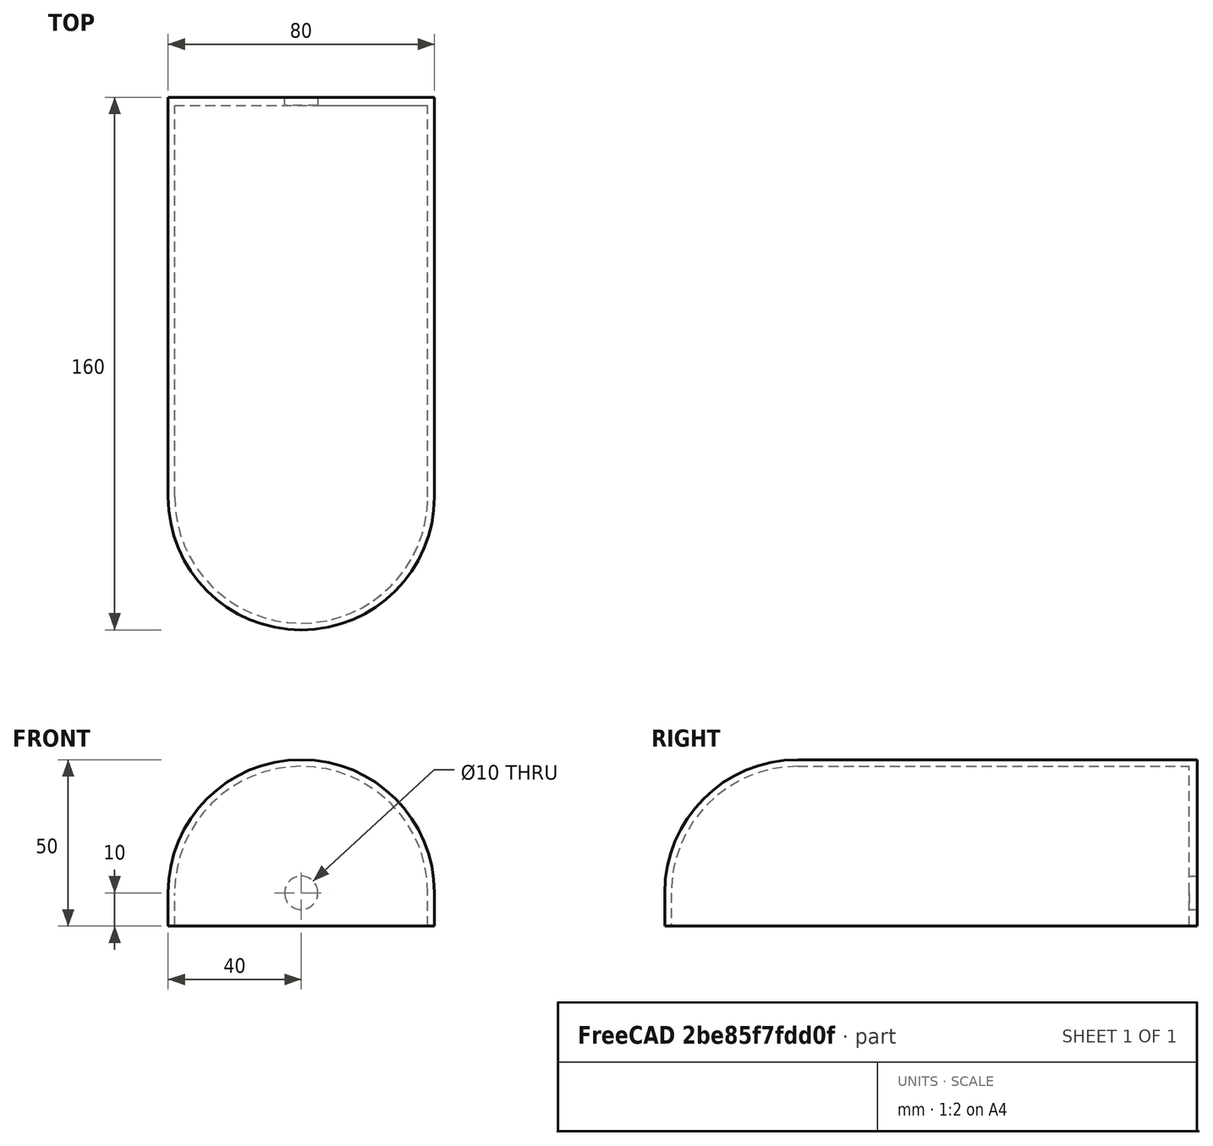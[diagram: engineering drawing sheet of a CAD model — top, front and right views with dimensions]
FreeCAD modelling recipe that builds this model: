
FCSTD DOCUMENT  (FreeCAD 0.20R29177 +426 (Git))
Label: Cabeza de lampara
License: All rights reserved
LicenseURL: http://en.wikipedia.org/wiki/All_rights_reserved
objects: Part::Cylinder×7, Part::Cut×6, Part::Box×3, Part::Sphere×2, Part::MultiFuse×2
note: 20 computed .brp shape members not serialized (recipe doc carries the construction recipe); baked Part::Feature solids carry a one-line shape summary decoded from their .brp

FEATURE [Part::Box] Box  label="Soporte parte inferior"
  AttacherType = Attacher::AttachEngine3D
  Height = 10
  Length = 76
  Placement = pos=(2,17.5,30) rot=(0,0,1;0rad)
  Width = 2.5
FEATURE [Part::Cylinder] Cylinder  label="Cilindro superior mayor"
  Angle = 180
  AttacherType = Attacher::AttachEngine3D
  FirstAngle = 0
  Height = 120
  Placement = pos=(40,20,40) rot=(1,0,0;1.5708rad)
  Radius = 40
  SecondAngle = 0
FEATURE [Part::Sphere] Sphere  label="Esfera mayor"
  Angle1 = -90
  Angle2 = 90
  Angle3 = 180
  AttacherType = Attacher::AttachEngine3D
  Placement = pos=(40,-100,40) rot=(1,0,0;1.5708rad)
  Radius = 40
FEATURE [Part::Box] Box001  label="Rectangulo mayor"
  AttacherType = Attacher::AttachEngine3D
  Height = 10
  Length = 80
  Placement = pos=(0,-100,30) rot=(0,0,1;0rad)
  Width = 120
FEATURE [Part::Cylinder] Cylinder001  label="Cilindro mayor"
  Angle = 180
  AttacherType = Attacher::AttachEngine3D
  FirstAngle = 0
  Height = 10
  Placement = pos=(40,-100,30) rot=(0,0,1;3.14159rad)
  Radius = 40
  SecondAngle = 0
FEATURE [Part::Cylinder] Cylinder002  label="Cilindro menor"
  Angle = 180
  AttacherType = Attacher::AttachEngine3D
  FirstAngle = 0
  Height = 10
  Placement = pos=(40,-100,30) rot=(0,0,1;3.14159rad)
  Radius = 38
  SecondAngle = 0
FEATURE [Part::Box] Box002  label="Rectangulo menor"
  AttacherType = Attacher::AttachEngine3D
  Height = 10
  Length = 76
  Placement = pos=(2,-100,30) rot=(0,0,1;0rad)
  Width = 120
FEATURE [Part::Sphere] Sphere001  label="Esfera menor"
  Angle1 = -90
  Angle2 = 90
  Angle3 = 180
  AttacherType = Attacher::AttachEngine3D
  Placement = pos=(40,-100,40) rot=(1,0,0;1.5708rad)
  Radius = 38
FEATURE [Part::Cylinder] Cylinder003  label="Cilindro superior menor"
  Angle = 180
  AttacherType = Attacher::AttachEngine3D
  FirstAngle = 0
  Height = 120
  Placement = pos=(40,20,40) rot=(1,0,0;1.5708rad)
  Radius = 38
  SecondAngle = 0
FEATURE [Part::Cut] Cut  label="Bordes"
  Base = -> Box001
  Tool = -> Box002
FEATURE [Part::Cut] Cut001  label="Techo"
  Base = -> Cylinder
  Tool = -> Cylinder003
FEATURE [Part::Cut] Cut002  label="Cupula pendiente de corte"
  Base = -> Sphere
  Tool = -> Sphere001
FEATURE [Part::Cut] Cut003  label="Borde de cupula"
  Base = -> Cylinder001
  Tool = -> Cylinder002
FEATURE [Part::Cylinder] Cylinder004  label="Cilindro superior mayor 01"
  Angle = 180
  AttacherType = Attacher::AttachEngine3D
  FirstAngle = 0
  Height = 120
  Placement = pos=(40,20,40) rot=(1,0,0;1.5708rad)
  Radius = 40
  SecondAngle = 0
FEATURE [Part::Cut] Cut004  label="Cupula cortada"
  Base = -> Cut002
  Tool = -> Cylinder004
FEATURE [Part::Cylinder] Cylinder005  label="Soporte para superior"
  Angle = 180
  AttacherType = Attacher::AttachEngine3D
  FirstAngle = 0
  Height = 2.5
  Placement = pos=(40,17.5,40) rot=(0,0.707107,0.707107;3.14159rad)
  Radius = 38
  SecondAngle = 0
FEATURE [Part::Cylinder] Cylinder006  label="Agujero"
  Angle = 360
  AttacherType = Attacher::AttachEngine3D
  FirstAngle = 0
  Height = 17
  Placement = pos=(40,24,40) rot=(1,0,0;1.5708rad)
  Radius = 5
  SecondAngle = 0
FEATURE [Part::MultiFuse] Fusion  label="Soporte"
  Shapes = -> [Box,Cylinder005]
FEATURE [Part::Cut] Cut005  label="Soporte con agujero"
  Base = -> Fusion
  Tool = -> Cylinder006
FEATURE [Part::MultiFuse] Fusion001  label="Cabeza de lampara terminada"
  Shapes = -> [Cut,Cut001,Cut003,Cut004,Cut005]
